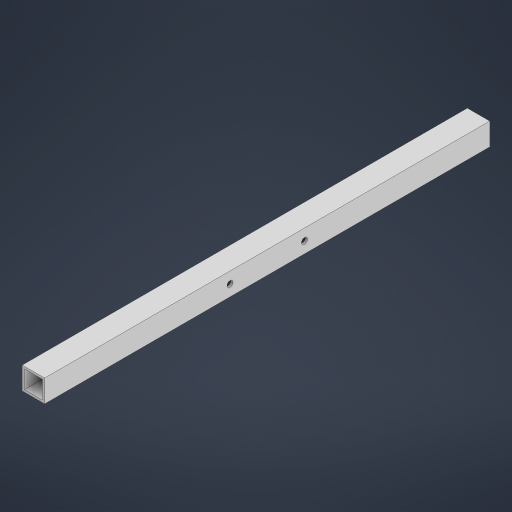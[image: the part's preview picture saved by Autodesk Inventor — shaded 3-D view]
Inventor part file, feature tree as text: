
AUTODESK INVENTOR PART (.ipt)
format: ipt  version: 2024 (Build 280153000, 153)  size: 200,192 bytes
history: native  units: mm
features: extrude x3, sketch x3, other x1
ambient origin geometry x8: Origin, YZ Plane, XZ Plane, XY Plane, X Axis, Y Axis, Z Axis, Center Point
bodies: Body1 (feature_tree)
feature tree (7):
  other  "Sólido1"
  extrude  "Extrusión1"  Depth=15.0mm
  extrude  "Extrusión2"  Depth=1.5mm
  extrude  "Extrusión3"  Depth=1.5mm
  sketch  "Boceto1"  dims[d0=15.0mm d1=15.0mm]
  sketch  "Boceto2"  dims[d2=1.5mm d3=1.5mm]
  sketch  "Boceto3"  dims[d4=1.5mm d5=1.5mm d6=298.4mm d7=0.0mm d8=4.0mm d9=4.0mm d10=7.5mm d11=7.5mm d12=50.0mm d13=124.2mm d14=10.0mm d15=0.0mm d16=4.0mm d17=4.0mm d18=100.0mm d19=99.2mm d20=10.0mm d21=0.0mm]
